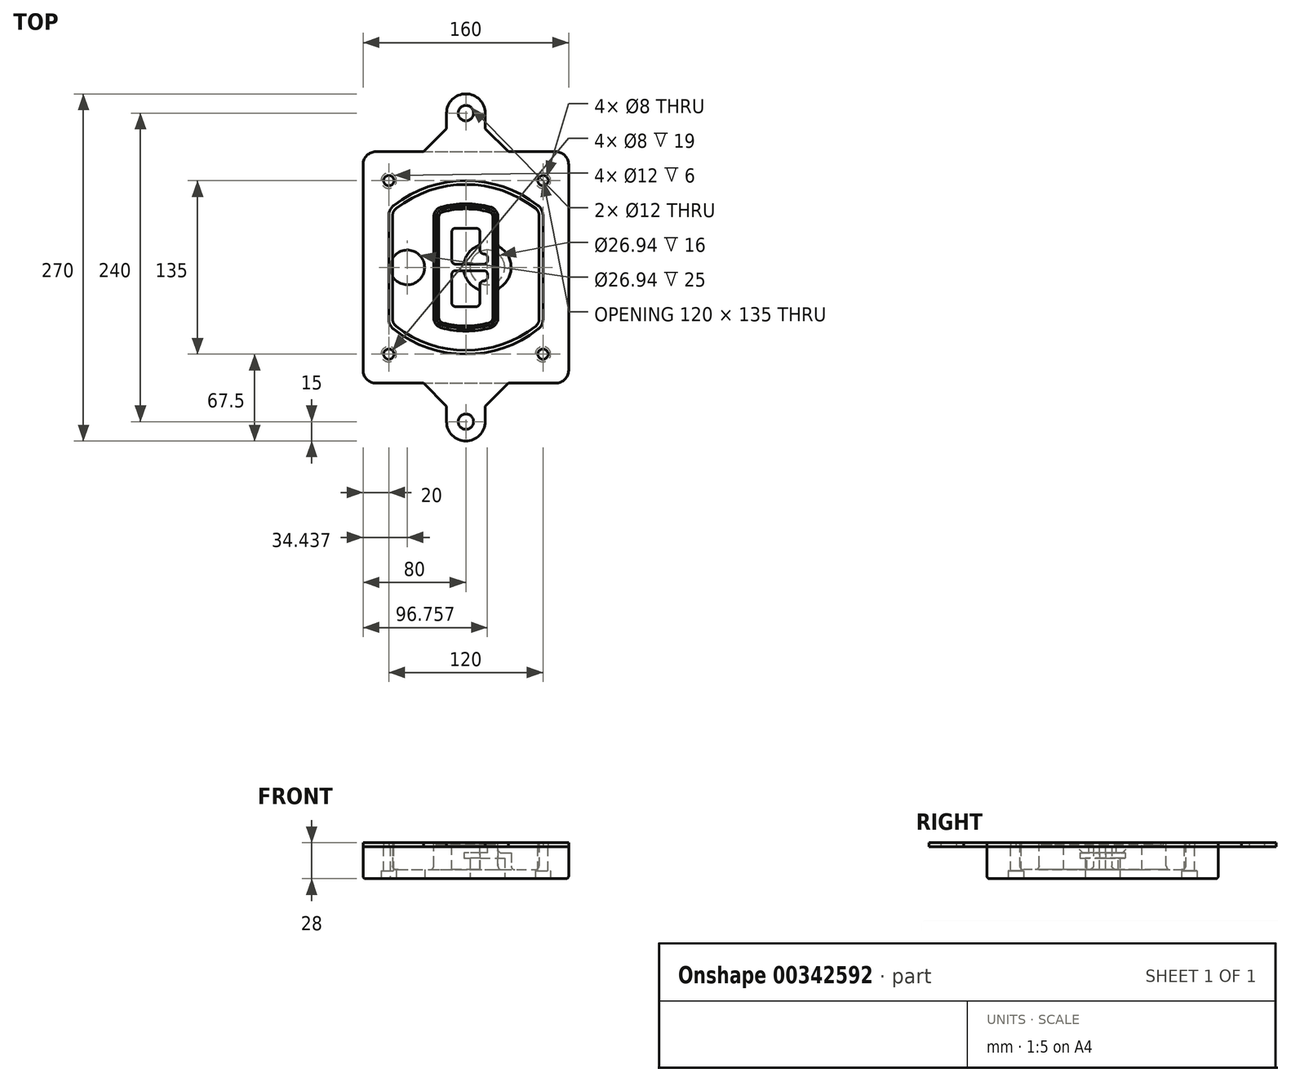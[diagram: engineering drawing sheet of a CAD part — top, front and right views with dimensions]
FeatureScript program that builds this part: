
annotation { "Feature Type Name" : "Feature", "Feature Type Description" : "" }
export const myFeature = defineFeature(function(context is Context, id is Id, definition is map)
    precondition{}
    {
        {
            var Q0;
            Q0=qCreatedBy(makeId("Top.planeOp"),FACE);
            var sketch = newSketch(context, id + "F0", { "sketchPlane" : qUnion([Q0])});
            skPoint(sketch, "E0.rect.middle", {"position": v(0, 0) * mm});
            skLineSegment(sketch, "E1.bottom", {"start": v(-70, -90) * mm, "end": v(70, -90) * mm});
            skLineSegment(sketch, "E1.top", {"start": v(-70, 90) * mm, "end": v(70, 90) * mm});
            skLineSegment(sketch, "E1.left", {"start": v(-80, -80) * mm, "end": v(-80, 80) * mm});
            skLineSegment(sketch, "E1.right", {"start": v(80, -80) * mm, "end": v(80, 80) * mm});
            skLineSegment(sketch, "E2", {"start": v(-80, 90) * mm, "end": v(80, -90) * mm, "construction": true});
            skLineSegment(sketch, "E3", {"start": v(80, 90) * mm, "end": v(-80, -90) * mm, "construction": true});
            skCircle(sketch, "E4", {"center": v(-60, 67.5) * mm, "radius": 4 * mm});
            skCircle(sketch, "E5", {"center": v(60, 67.5) * mm, "radius": 4 * mm});
            skCircle(sketch, "E6", {"center": v(60, -67.5) * mm, "radius": 4 * mm});
            skCircle(sketch, "E7", {"center": v(-60, -67.5) * mm, "radius": 4 * mm});
            skLineSegment(sketch, "E8", {"start": v(-60, 67.5) * mm, "end": v(60, 67.5) * mm, "construction": true});
            skLineSegment(sketch, "E9", {"start": v(60, 67.5) * mm, "end": v(60, -67.5) * mm, "construction": true});
            skLineSegment(sketch, "E10", {"start": v(60, -67.5) * mm, "end": v(-60, -67.5) * mm, "construction": true});
            skLineSegment(sketch, "E11", {"start": v(-60, -67.5) * mm, "end": v(-60, 67.5) * mm, "construction": true});
            skLineSegment(sketch, "E12", {"start": v(-60, 40.3) * mm, "end": v(-60, -40.3) * mm});
            skLineSegment(sketch, "E13", {"start": v(60, 40.3) * mm, "end": v(60, -40.3) * mm});
            skArc(sketch, "E14", {"start": v(56.15, 48.18) * mm, "mid": v(0, 67.5) * mm, "end": v(-56.15, 48.18) * mm});
            skArc(sketch, "E15", {"start": v(-56.15, -48.18) * mm, "mid": v(0, -67.5) * mm, "end": v(56.15, -48.18) * mm});
            skLineSegment(sketch, "E16", {"start": v(-60, 0) * mm, "end": v(60, 0) * mm, "construction": true});
            skPoint(sketch, "E17.visualSharp", {"position": v(-60, -45) * mm});
            skArc(sketch, "E17.filletArc", {"start": v(-60, -40.3) * mm, "mid": v(-58.99, -44.68) * mm, "end": v(-56.15, -48.18) * mm});
            skPoint(sketch, "E18.visualSharp", {"position": v(-60, 45) * mm});
            skArc(sketch, "E18.filletArc", {"start": v(-56.15, 48.18) * mm, "mid": v(-58.99, 44.68) * mm, "end": v(-60, 40.3) * mm});
            skPoint(sketch, "E19.visualSharp", {"position": v(60, 45) * mm});
            skArc(sketch, "E19.filletArc", {"start": v(60, 40.3) * mm, "mid": v(58.99, 44.68) * mm, "end": v(56.15, 48.18) * mm});
            skPoint(sketch, "E20.visualSharp", {"position": v(60, -45) * mm});
            skArc(sketch, "E20.filletArc", {"start": v(56.15, -48.18) * mm, "mid": v(58.99, -44.68) * mm, "end": v(60, -40.3) * mm});
            skPoint(sketch, "E21.visualSharp", {"position": v(-80, 90) * mm});
            skArc(sketch, "E21.filletArc", {"start": v(-70, 90) * mm, "mid": v(-77.07, 87.07) * mm, "end": v(-80, 80) * mm});
            skPoint(sketch, "E22.visualSharp", {"position": v(80, 90) * mm});
            skArc(sketch, "E22.filletArc", {"start": v(80, 80) * mm, "mid": v(77.07, 87.07) * mm, "end": v(70, 90) * mm});
            skPoint(sketch, "E23.visualSharp", {"position": v(80, -90) * mm});
            skArc(sketch, "E23.filletArc", {"start": v(70, -90) * mm, "mid": v(77.07, -87.07) * mm, "end": v(80, -80) * mm});
            skPoint(sketch, "E24.visualSharp", {"position": v(-80, -90) * mm});
            skArc(sketch, "E24.filletArc", {"start": v(-80, -80) * mm, "mid": v(-77.07, -87.07) * mm, "end": v(-70, -90) * mm});
            skArc(sketch, "E25.0", {"start": v(57, 40.3) * mm, "mid": v(56.3, 43.36) * mm, "end": v(54.3, 45.81) * mm});
            skLineSegment(sketch, "E25.1", {"start": v(57, 40.3) * mm, "end": v(57, -40.3) * mm});
            skArc(sketch, "E25.2", {"start": v(54.3, -45.81) * mm, "mid": v(56.3, -43.36) * mm, "end": v(57, -40.3) * mm});
            skArc(sketch, "E25.3", {"start": v(-54.3, -45.81) * mm, "mid": v(0, -64.5) * mm, "end": v(54.3, -45.81) * mm});
            skArc(sketch, "E25.4", {"start": v(-57, -40.3) * mm, "mid": v(-56.3, -43.36) * mm, "end": v(-54.3, -45.81) * mm});
            skArc(sketch, "E25.5", {"start": v(54.3, 45.81) * mm, "mid": v(0, 64.5) * mm, "end": v(-54.3, 45.81) * mm});
            skLineSegment(sketch, "E25.6", {"start": v(-57, 40.3) * mm, "end": v(-57, -40.3) * mm});
            skArc(sketch, "E25.7", {"start": v(-54.3, 45.81) * mm, "mid": v(-56.3, 43.36) * mm, "end": v(-57, 40.3) * mm});
            skArc(sketch, "E26.0", {"start": v(-58.62, 51.33) * mm, "mid": v(-62.58, 46.43) * mm, "end": v(-64, 40.3) * mm});
            skArc(sketch, "E26.1", {"start": v(58.62, 51.33) * mm, "mid": v(0, 71.5) * mm, "end": v(-58.62, 51.33) * mm});
            skArc(sketch, "E26.2", {"start": v(64, 40.3) * mm, "mid": v(62.58, 46.43) * mm, "end": v(58.62, 51.33) * mm});
            skLineSegment(sketch, "E26.3", {"start": v(64, 40.3) * mm, "end": v(64, -40.3) * mm});
            skArc(sketch, "E26.4", {"start": v(58.62, -51.33) * mm, "mid": v(62.58, -46.43) * mm, "end": v(64, -40.3) * mm});
            skLineSegment(sketch, "E26.5", {"start": v(-64, 40.3) * mm, "end": v(-64, -40.3) * mm});
            skArc(sketch, "E26.6", {"start": v(-58.62, -51.33) * mm, "mid": v(0, -71.5) * mm, "end": v(58.62, -51.33) * mm});
            skArc(sketch, "E26.7", {"start": v(-64, -40.3) * mm, "mid": v(-62.58, -46.43) * mm, "end": v(-58.62, -51.33) * mm});
            skSolve(sketch);
        }
        {
            var Q0;
            Q0=makeQuery(id+"F0.imprint","IMPRINT",FACE,{"disambiguationData":[TD([[makeQuery(id+"F0.imprint","IMPRINT",EDGE,{"derivedFrom":sQuery(id+"F0.wireOp",EDGE,"E1.bottom")}),1.0]])]});
            var Q1;
            Q1=makeQuery(id+"F0.imprint","IMPRINT",FACE,{"disambiguationData":[TD([[makeQuery(id+"F0.imprint","IMPRINT",EDGE,{"derivedFrom":sQuery(id+"F0.wireOp",EDGE,"E12")}),1.0]])]});
            var Q2;
            Q2=makeQuery(id+"F0.imprint","IMPRINT",FACE,{"disambiguationData":[TD([[makeQuery(id+"F0.imprint","IMPRINT",EDGE,{"derivedFrom":sQuery(id+"F0.wireOp",EDGE,"E25.0")}),1.0]])]});
            var Q3;
            Q3=makeQuery(id+"F0.imprint","IMPRINT",FACE,{"disambiguationData":[TD([[makeQuery(id+"F0.imprint","IMPRINT",EDGE,{"derivedFrom":sQuery(id+"F0.wireOp",EDGE,"E12")}),-1.0]])]});
            extrude(context, id + "F1", {"entities" : qUnion([Q0, Q1, Q2, Q3]), "oppositeDirection" : true, "depth" : 25 * mm});
        }
        {
            var Q0;
            Q0=makeQuery(id+"F0.imprint","IMPRINT",FACE,{"disambiguationData":[TD([[makeQuery(id+"F0.imprint","IMPRINT",EDGE,{"derivedFrom":sQuery(id+"F0.wireOp",EDGE,"E12")}),1.0]])]});
            extrude(context, id + "F2", {"entities" : qUnion([Q0]), "operationType" : NewBodyOperationType.ADD, "depth" : 3 * mm});
        }
        {
            var Q0;
            Q0=makeQuery(id+"F0.imprint","IMPRINT",FACE,{"disambiguationData":[TD([[makeQuery(id+"F0.imprint","IMPRINT",EDGE,{"derivedFrom":sQuery(id+"F0.wireOp",EDGE,"E25.0")}),1.0]])]});
            extrude(context, id + "F3", {"entities" : qUnion([Q0]), "operationType" : NewBodyOperationType.REMOVE, "oppositeDirection" : true, "depth" : 18 * mm});
        }
        {
            var Q0;
            Q0=makeQuery(id+"F2.opExtrude","CAP_FACE",FACE,{"disambiguationData":[OSD([sQuery(id+"F0.wireOp",EDGE,"E12"),sQuery(id+"F0.wireOp",EDGE,"E13"),sQuery(id+"F0.wireOp",EDGE,"E14"),sQuery(id+"F0.wireOp",EDGE,"E15"),sQuery(id+"F0.wireOp",EDGE,"E17.filletArc"),sQuery(id+"F0.wireOp",EDGE,"E18.filletArc"),sQuery(id+"F0.wireOp",EDGE,"E19.filletArc"),sQuery(id+"F0.wireOp",EDGE,"E20.filletArc"),sQuery(id+"F0.wireOp",EDGE,"E25.0"),sQuery(id+"F0.wireOp",EDGE,"E25.1"),sQuery(id+"F0.wireOp",EDGE,"E25.2"),sQuery(id+"F0.wireOp",EDGE,"E25.3"),sQuery(id+"F0.wireOp",EDGE,"E25.4"),sQuery(id+"F0.wireOp",EDGE,"E25.5"),sQuery(id+"F0.wireOp",EDGE,"E25.6"),sQuery(id+"F0.wireOp",EDGE,"E25.7")])],"isStart":false});
            var sketch = newSketch(context, id + "F4", { "sketchPlane" : qUnion([Q0])});
            skArc(sketch, "E27.0", {"start": v(-19.08, -46.97) * mm, "mid": v(0, -49.5) * mm, "end": v(19.08, -46.97) * mm});
            skArc(sketch, "E28.0", {"start": v(19.08, 46.97) * mm, "mid": v(0, 49.5) * mm, "end": v(-19.08, 46.97) * mm});
            skLineSegment(sketch, "E29", {"start": v(-25, 39.25) * mm, "end": v(-25, -39.25) * mm});
            skLineSegment(sketch, "E30", {"start": v(25, 39.25) * mm, "end": v(25, -39.25) * mm});
            skLineSegment(sketch, "E31", {"start": v(-25, 45.1) * mm, "end": v(25, 45.1) * mm, "construction": true});
            skLineSegment(sketch, "E32", {"start": v(-25, -45.1) * mm, "end": v(25, -45.1) * mm, "construction": true});
            skPoint(sketch, "E33.visualSharp", {"position": v(-25, 45.1) * mm});
            skArc(sketch, "E33.filletArc", {"start": v(-19.08, 46.97) * mm, "mid": v(-23.35, 44.11) * mm, "end": v(-25, 39.25) * mm});
            skPoint(sketch, "E34.visualSharp", {"position": v(25, 45.1) * mm});
            skArc(sketch, "E34.filletArc", {"start": v(25, 39.25) * mm, "mid": v(23.35, 44.11) * mm, "end": v(19.08, 46.97) * mm});
            skPoint(sketch, "E35.visualSharp", {"position": v(25, -45.1) * mm});
            skArc(sketch, "E35.filletArc", {"start": v(19.08, -46.97) * mm, "mid": v(23.35, -44.11) * mm, "end": v(25, -39.25) * mm});
            skPoint(sketch, "E36.visualSharp", {"position": v(-25, -45.1) * mm});
            skArc(sketch, "E36.filletArc", {"start": v(-25, -39.25) * mm, "mid": v(-23.35, -44.11) * mm, "end": v(-19.08, -46.97) * mm});
            skArc(sketch, "E37.0", {"start": v(54.3, 45.81) * mm, "mid": v(0, 64.5) * mm, "end": v(-54.3, 45.81) * mm});
            skArc(sketch, "E37.1", {"start": v(-54.3, 45.81) * mm, "mid": v(-56.3, 43.36) * mm, "end": v(-57, 40.3) * mm});
            skLineSegment(sketch, "E37.2", {"start": v(-57, 40.3) * mm, "end": v(-57, -40.3) * mm});
            skArc(sketch, "E37.3", {"start": v(-57, -40.3) * mm, "mid": v(-56.3, -43.36) * mm, "end": v(-54.3, -45.81) * mm});
            skArc(sketch, "E37.4", {"start": v(-54.3, -45.81) * mm, "mid": v(0, -64.5) * mm, "end": v(54.3, -45.81) * mm});
            skArc(sketch, "E37.5", {"start": v(54.3, -45.81) * mm, "mid": v(56.3, -43.36) * mm, "end": v(57, -40.3) * mm});
            skLineSegment(sketch, "E37.6", {"start": v(57, 40.3) * mm, "end": v(57, -40.3) * mm});
            skArc(sketch, "E37.7", {"start": v(57, 40.3) * mm, "mid": v(56.3, 43.36) * mm, "end": v(54.3, 45.81) * mm});
            skLineSegment(sketch, "E38.0", {"start": v(23, 39.25) * mm, "end": v(23, -39.25) * mm});
            skArc(sketch, "E38.1", {"start": v(18.56, -45.04) * mm, "mid": v(21.76, -42.9) * mm, "end": v(23, -39.25) * mm});
            skArc(sketch, "E38.2", {"start": v(-18.56, -45.04) * mm, "mid": v(0, -47.5) * mm, "end": v(18.56, -45.04) * mm});
            skArc(sketch, "E38.3", {"start": v(-23, -39.25) * mm, "mid": v(-21.76, -42.9) * mm, "end": v(-18.56, -45.04) * mm});
            skLineSegment(sketch, "E38.4", {"start": v(-23, 39.25) * mm, "end": v(-23, -39.25) * mm});
            skArc(sketch, "E38.5", {"start": v(23, 39.25) * mm, "mid": v(21.76, 42.9) * mm, "end": v(18.56, 45.04) * mm});
            skArc(sketch, "E38.6", {"start": v(-18.56, 45.04) * mm, "mid": v(-21.76, 42.9) * mm, "end": v(-23, 39.25) * mm});
            skArc(sketch, "E38.7", {"start": v(18.56, 45.04) * mm, "mid": v(0, 47.5) * mm, "end": v(-18.56, 45.04) * mm});
            skArc(sketch, "E39.0", {"start": v(21, 39.25) * mm, "mid": v(20.18, 41.68) * mm, "end": v(18.04, 43.1) * mm});
            skLineSegment(sketch, "E39.1", {"start": v(21, 39.25) * mm, "end": v(21, -39.25) * mm});
            skArc(sketch, "E39.2", {"start": v(18.04, -43.1) * mm, "mid": v(20.18, -41.68) * mm, "end": v(21, -39.25) * mm});
            skArc(sketch, "E39.3", {"start": v(-18.04, -43.1) * mm, "mid": v(0, -45.5) * mm, "end": v(18.04, -43.1) * mm});
            skArc(sketch, "E39.4", {"start": v(-21, -39.25) * mm, "mid": v(-20.18, -41.68) * mm, "end": v(-18.04, -43.1) * mm});
            skArc(sketch, "E39.5", {"start": v(18.04, 43.1) * mm, "mid": v(0, 45.5) * mm, "end": v(-18.04, 43.1) * mm});
            skLineSegment(sketch, "E39.6", {"start": v(-21, 39.25) * mm, "end": v(-21, -39.25) * mm});
            skArc(sketch, "E39.7", {"start": v(-18.04, 43.1) * mm, "mid": v(-20.18, 41.68) * mm, "end": v(-21, 39.25) * mm});
            skLineSegment(sketch, "E40", {"start": v(-25, 0) * mm, "end": v(25, 0) * mm, "construction": true});
            skLineSegment(sketch, "E41", {"start": v(-11, 5.5) * mm, "end": v(-11, 27.5) * mm});
            skLineSegment(sketch, "E42", {"start": v(-8, 30.5) * mm, "end": v(8, 30.5) * mm});
            skLineSegment(sketch, "E43", {"start": v(11, 27.5) * mm, "end": v(11, 13.5) * mm});
            skLineSegment(sketch, "E44", {"start": v(14, 10.5) * mm, "end": v(14, 10.5) * mm});
            skLineSegment(sketch, "E45", {"start": v(17, 7.5) * mm, "end": v(17, 5.5) * mm});
            skLineSegment(sketch, "E46", {"start": v(14, 2.5) * mm, "end": v(-8, 2.5) * mm});
            skPoint(sketch, "E47.visualSharp", {"position": v(-11, 30.5) * mm});
            skArc(sketch, "E47.filletArc", {"start": v(-8, 30.5) * mm, "mid": v(-10.12, 29.62) * mm, "end": v(-11, 27.5) * mm});
            skPoint(sketch, "E48.visualSharp", {"position": v(11, 30.5) * mm});
            skArc(sketch, "E48.filletArc", {"start": v(11, 27.5) * mm, "mid": v(10.12, 29.62) * mm, "end": v(8, 30.5) * mm});
            skPoint(sketch, "E49.visualSharp", {"position": v(11, 10.5) * mm});
            skArc(sketch, "E49.filletArc", {"start": v(11, 13.5) * mm, "mid": v(11.88, 11.38) * mm, "end": v(14, 10.5) * mm});
            skPoint(sketch, "E50.visualSharp", {"position": v(17, 10.5) * mm});
            skArc(sketch, "E50.filletArc", {"start": v(17, 7.5) * mm, "mid": v(16.12, 9.62) * mm, "end": v(14, 10.5) * mm});
            skPoint(sketch, "E51.visualSharp", {"position": v(17, 2.5) * mm});
            skArc(sketch, "E51.filletArc", {"start": v(14, 2.5) * mm, "mid": v(16.12, 3.38) * mm, "end": v(17, 5.5) * mm});
            skPoint(sketch, "E52.visualSharp", {"position": v(-11, 2.5) * mm});
            skArc(sketch, "E52.filletArc", {"start": v(-11, 5.5) * mm, "mid": v(-10.12, 3.38) * mm, "end": v(-8, 2.5) * mm});
            skLineSegment(sketch, "E53.0.MirrorCS", {"start": v(14, -2.5) * mm, "end": v(-8, -2.5) * mm});
            skArc(sketch, "E54.0.MirrorCS", {"start": v(-11, -5.5) * mm, "mid": v(-10.12, -3.38) * mm, "end": v(-8, -2.5) * mm});
            skLineSegment(sketch, "E55.0.MirrorCS", {"start": v(-11, -5.5) * mm, "end": v(-11, -27.5) * mm});
            skArc(sketch, "E56.0.MirrorCS", {"start": v(-8, -30.5) * mm, "mid": v(-10.12, -29.62) * mm, "end": v(-11, -27.5) * mm});
            skLineSegment(sketch, "E57.0.MirrorCS", {"start": v(-8, -30.5) * mm, "end": v(8, -30.5) * mm});
            skArc(sketch, "E58.0.MirrorCS", {"start": v(11, -27.5) * mm, "mid": v(10.12, -29.62) * mm, "end": v(8, -30.5) * mm});
            skLineSegment(sketch, "E59.0.MirrorCS", {"start": v(11, -27.5) * mm, "end": v(11, -13.5) * mm});
            skArc(sketch, "E60.0.MirrorCS", {"start": v(11, -13.5) * mm, "mid": v(11.88, -11.38) * mm, "end": v(14, -10.5) * mm});
            skArc(sketch, "E61.0.MirrorCS", {"start": v(17, -7.5) * mm, "mid": v(16.12, -9.62) * mm, "end": v(14, -10.5) * mm});
            skLineSegment(sketch, "E62.0.MirrorCS", {"start": v(17, -7.5) * mm, "end": v(17, -5.5) * mm});
            skArc(sketch, "E63.0.MirrorCS", {"start": v(14, -2.5) * mm, "mid": v(16.12, -3.38) * mm, "end": v(17, -5.5) * mm});
            skSolve(sketch);
        }
        {
            var Q0;
            Q0=makeQuery(id+"F4.imprint","IMPRINT",FACE,{"disambiguationData":[TD([[makeQuery(id+"F4.imprint","IMPRINT",EDGE,{"derivedFrom":sQuery(id+"F4.wireOp",EDGE,"E27.0")}),1.0]])]});
            var Q1;
            Q1=makeQuery(id+"F4.imprint","IMPRINT",FACE,{"disambiguationData":[TD([[makeQuery(id+"F4.imprint","IMPRINT",EDGE,{"derivedFrom":sQuery(id+"F4.wireOp",EDGE,"E38.0")}),-1.0]])]});
            var Q2;
            Q2=makeQuery(id+"F4.imprint","IMPRINT",FACE,{"disambiguationData":[TD([[makeQuery(id+"F4.imprint","IMPRINT",EDGE,{"derivedFrom":sQuery(id+"F4.wireOp",EDGE,"E39.0")}),1.0]])]});
            extrude(context, id + "F5", {"entities" : qUnion([Q0, Q1, Q2]), "operationType" : NewBodyOperationType.ADD, "endBound" : BoundingType.UP_TO_NEXT, "oppositeDirection" : true, "depth" : 25 * mm});
        }
        {
            var Q0;
            Q0=makeQuery(id+"F4.imprint","IMPRINT",FACE,{"disambiguationData":[TD([[makeQuery(id+"F4.imprint","IMPRINT",EDGE,{"derivedFrom":sQuery(id+"F4.wireOp",EDGE,"E38.0")}),-1.0]])]});
            extrude(context, id + "F6", {"entities" : qUnion([Q0]), "operationType" : NewBodyOperationType.REMOVE, "oppositeDirection" : true, "depth" : 2 * mm});
        }
        {
            var Q0;
            Q0=makeQuery(id+"F1.opExtrude","CAP_FACE",FACE,{"disambiguationData":[OSD([sQuery(id+"F0.wireOp",EDGE,"E1.bottom"),sQuery(id+"F0.wireOp",EDGE,"E1.top"),sQuery(id+"F0.wireOp",EDGE,"E1.left"),sQuery(id+"F0.wireOp",EDGE,"E1.right"),sQuery(id+"F0.wireOp",EDGE,"E4"),sQuery(id+"F0.wireOp",EDGE,"E5"),sQuery(id+"F0.wireOp",EDGE,"E6"),sQuery(id+"F0.wireOp",EDGE,"E7"),sQuery(id+"F0.wireOp",EDGE,"E21.filletArc"),sQuery(id+"F0.wireOp",EDGE,"E22.filletArc"),sQuery(id+"F0.wireOp",EDGE,"E23.filletArc"),sQuery(id+"F0.wireOp",EDGE,"E24.filletArc")])],"isStart":false});
            var sketch = newSketch(context, id + "F7", { "sketchPlane" : qUnion([Q0])});
            skCircle(sketch, "E64", {"center": v(16.76, 0) * mm, "radius": 13.47 * mm});
            skCircle(sketch, "E65", {"center": v(-45.56, 0) * mm, "radius": 13.47 * mm});
            skLineSegment(sketch, "E66", {"start": v(80, 0) * mm, "end": v(-80, 0) * mm});
            skCircle(sketch, "E67", {"center": v(16.76, 0) * mm, "radius": 18.47 * mm});
            skCircle(sketch, "E68", {"center": v(60, -67.5) * mm, "radius": 6 * mm});
            skCircle(sketch, "E69", {"center": v(-60, -67.5) * mm, "radius": 6 * mm});
            skCircle(sketch, "E70", {"center": v(-60, 67.5) * mm, "radius": 6 * mm});
            skCircle(sketch, "E71", {"center": v(60, 67.5) * mm, "radius": 6 * mm});
            skSolve(sketch);
        }
        {
            var Q0;
            {var subQ1=sQuery(id+"F7.wireOp",EDGE,"E66");var subQ4=sQuery(id+"F7.wireOp",EDGE,"E64");var subQ6=makeQuery(id+"F7.imprint","INTERSECT",VERTEX,{"disambiguationData":[OD(0.0)],"derivedFrom":[subQ4,subQ1]});Q0=makeQuery(id+"F7.imprint","IMPRINT",FACE,{"disambiguationData":[TD([[makeQuery(id+"F7.imprint","IMPRINT",EDGE,{"disambiguationData":[TD([[subQ6,-1.0]])],"derivedFrom":subQ4}),-1.0]])]});}
            var Q1;
            {var subQ0=sQuery(id+"F7.wireOp",EDGE,"E66");var subQ1=sQuery(id+"F7.wireOp",EDGE,"E64");var subQ3=makeQuery(id+"F7.imprint","INTERSECT",VERTEX,{"disambiguationData":[OD(0.0)],"derivedFrom":[subQ1,subQ0]});Q1=makeQuery(id+"F7.imprint","IMPRINT",FACE,{"disambiguationData":[TD([[makeQuery(id+"F7.imprint","IMPRINT",EDGE,{"disambiguationData":[TD([[subQ3,-1.0]])],"derivedFrom":subQ1}),1.0]])]});}
            var Q2;
            {var subQ0=sQuery(id+"F7.wireOp",EDGE,"E66");var subQ1=sQuery(id+"F7.wireOp",EDGE,"E64");var subQ3=makeQuery(id+"F7.imprint","INTERSECT",VERTEX,{"disambiguationData":[OD(0.0)],"derivedFrom":[subQ1,subQ0]});Q2=makeQuery(id+"F7.imprint","IMPRINT",FACE,{"disambiguationData":[TD([[makeQuery(id+"F7.imprint","IMPRINT",EDGE,{"disambiguationData":[TD([[subQ3,1.0]])],"derivedFrom":subQ1}),1.0]])]});}
            var Q3;
            {var subQ1=sQuery(id+"F7.wireOp",EDGE,"E66");var subQ4=sQuery(id+"F7.wireOp",EDGE,"E64");var subQ6=makeQuery(id+"F7.imprint","INTERSECT",VERTEX,{"disambiguationData":[OD(0.0)],"derivedFrom":[subQ4,subQ1]});Q3=makeQuery(id+"F7.imprint","IMPRINT",FACE,{"disambiguationData":[TD([[makeQuery(id+"F7.imprint","IMPRINT",EDGE,{"disambiguationData":[TD([[subQ6,1.0]])],"derivedFrom":subQ4}),-1.0]])]});}
            extrude(context, id + "F8", {"entities" : qUnion([Q0, Q1, Q2, Q3]), "operationType" : NewBodyOperationType.ADD, "oppositeDirection" : true, "depth" : 20 * mm});
        }
        {
            var Q0;
            {var subQ0=sQuery(id+"F7.wireOp",EDGE,"E66");var subQ1=sQuery(id+"F7.wireOp",EDGE,"E64");var subQ3=makeQuery(id+"F7.imprint","INTERSECT",VERTEX,{"disambiguationData":[OD(0.0)],"derivedFrom":[subQ1,subQ0]});Q0=makeQuery(id+"F7.imprint","IMPRINT",FACE,{"disambiguationData":[TD([[makeQuery(id+"F7.imprint","IMPRINT",EDGE,{"disambiguationData":[TD([[subQ3,-1.0]])],"derivedFrom":subQ1}),1.0]])]});}
            var Q1;
            {var subQ0=sQuery(id+"F7.wireOp",EDGE,"E66");var subQ1=sQuery(id+"F7.wireOp",EDGE,"E64");var subQ3=makeQuery(id+"F7.imprint","INTERSECT",VERTEX,{"disambiguationData":[OD(0.0)],"derivedFrom":[subQ1,subQ0]});Q1=makeQuery(id+"F7.imprint","IMPRINT",FACE,{"disambiguationData":[TD([[makeQuery(id+"F7.imprint","IMPRINT",EDGE,{"disambiguationData":[TD([[subQ3,1.0]])],"derivedFrom":subQ1}),1.0]])]});}
            extrude(context, id + "F9", {"entities" : qUnion([Q0, Q1]), "operationType" : NewBodyOperationType.REMOVE, "oppositeDirection" : true, "depth" : 16 * mm});
        }
        {
            var Q0;
            {var subQ0=sQuery(id+"F7.wireOp",EDGE,"E66");var subQ1=sQuery(id+"F7.wireOp",EDGE,"E65");var subQ3=makeQuery(id+"F7.imprint","INTERSECT",VERTEX,{"disambiguationData":[OD(0.0)],"derivedFrom":[subQ1,subQ0]});Q0=makeQuery(id+"F7.imprint","IMPRINT",FACE,{"disambiguationData":[TD([[makeQuery(id+"F7.imprint","IMPRINT",EDGE,{"disambiguationData":[TD([[subQ3,-1.0]])],"derivedFrom":subQ1}),1.0]])]});}
            var Q1;
            {var subQ0=sQuery(id+"F7.wireOp",EDGE,"E66");var subQ1=sQuery(id+"F7.wireOp",EDGE,"E65");var subQ3=makeQuery(id+"F7.imprint","INTERSECT",VERTEX,{"disambiguationData":[OD(0.0)],"derivedFrom":[subQ1,subQ0]});Q1=makeQuery(id+"F7.imprint","IMPRINT",FACE,{"disambiguationData":[TD([[makeQuery(id+"F7.imprint","IMPRINT",EDGE,{"disambiguationData":[TD([[subQ3,1.0]])],"derivedFrom":subQ1}),1.0]])]});}
            extrude(context, id + "F10", {"entities" : qUnion([Q0, Q1]), "operationType" : NewBodyOperationType.REMOVE, "oppositeDirection" : true, "depth" : 25 * mm});
        }
        {
            var Q0;
            Q0=makeQuery(id+"F7.imprint","IMPRINT",FACE,{"disambiguationData":[TD([[makeQuery(id+"F7.imprint","IMPRINT",EDGE,{"derivedFrom":sQuery(id+"F7.wireOp",EDGE,"E68")}),1.0]])]});
            var Q1;
            Q1=makeQuery(id+"F7.imprint","IMPRINT",FACE,{"disambiguationData":[TD([[makeQuery(id+"F7.imprint","IMPRINT",EDGE,{"derivedFrom":makeQuery(id+"F1.opExtrude","CAP_EDGE",EDGE,{"disambiguationData":[OSD([sQuery(id+"F0.wireOp",EDGE,"E5")])],"isStart":false})}),-1.0]])]});
            var Q2;
            Q2=makeQuery(id+"F7.imprint","IMPRINT",FACE,{"disambiguationData":[TD([[makeQuery(id+"F7.imprint","IMPRINT",EDGE,{"derivedFrom":sQuery(id+"F7.wireOp",EDGE,"E69")}),1.0]])]});
            var Q3;
            Q3=makeQuery(id+"F7.imprint","IMPRINT",FACE,{"disambiguationData":[TD([[makeQuery(id+"F7.imprint","IMPRINT",EDGE,{"derivedFrom":makeQuery(id+"F1.opExtrude","CAP_EDGE",EDGE,{"disambiguationData":[OSD([sQuery(id+"F0.wireOp",EDGE,"E4")])],"isStart":false})}),-1.0]])]});
            var Q4;
            Q4=makeQuery(id+"F7.imprint","IMPRINT",FACE,{"disambiguationData":[TD([[makeQuery(id+"F7.imprint","IMPRINT",EDGE,{"derivedFrom":sQuery(id+"F7.wireOp",EDGE,"E70")}),1.0]])]});
            var Q5;
            Q5=makeQuery(id+"F7.imprint","IMPRINT",FACE,{"disambiguationData":[TD([[makeQuery(id+"F7.imprint","IMPRINT",EDGE,{"derivedFrom":makeQuery(id+"F1.opExtrude","CAP_EDGE",EDGE,{"disambiguationData":[OSD([sQuery(id+"F0.wireOp",EDGE,"E7")])],"isStart":false})}),-1.0]])]});
            var Q6;
            Q6=makeQuery(id+"F7.imprint","IMPRINT",FACE,{"disambiguationData":[TD([[makeQuery(id+"F7.imprint","IMPRINT",EDGE,{"derivedFrom":sQuery(id+"F7.wireOp",EDGE,"E71")}),1.0]])]});
            var Q7;
            Q7=makeQuery(id+"F7.imprint","IMPRINT",FACE,{"disambiguationData":[TD([[makeQuery(id+"F7.imprint","IMPRINT",EDGE,{"derivedFrom":makeQuery(id+"F1.opExtrude","CAP_EDGE",EDGE,{"disambiguationData":[OSD([sQuery(id+"F0.wireOp",EDGE,"E6")])],"isStart":false})}),-1.0]])]});
            extrude(context, id + "F11", {"entities" : qUnion([Q0, Q1, Q2, Q3, Q4, Q5, Q6, Q7]), "operationType" : NewBodyOperationType.REMOVE, "oppositeDirection" : true, "depth" : 6 * mm});
        }
        {
            var Q0;
            Q0=makeQuery(id+"F9.boolean.opBoolean","COPY",FACE,{"derivedFrom":makeQuery(id+"F9.opExtrude","CAP_FACE",FACE,{"disambiguationData":[OSD([sQuery(id+"F7.wireOp",EDGE,"E64")])],"isStart":false})});
            var sketch = newSketch(context, id + "F12", { "sketchPlane" : qUnion([Q0])});
            skArc(sketch, "E72.0", {"start": v(11, 17.55) * mm, "mid": v(2.57, 11.82) * mm, "end": v(-1.54, 2.5) * mm});
            skArc(sketch, "E72.1", {"start": v(-1.54, -2.5) * mm, "mid": v(2.57, -11.82) * mm, "end": v(11, -17.55) * mm});
            skLineSegment(sketch, "E73", {"start": v(-1.54, -2.5) * mm, "end": v(14, -2.5) * mm});
            skLineSegment(sketch, "E74.0", {"start": v(14, 2.5) * mm, "end": v(-1.54, 2.5) * mm});
            skArc(sketch, "E74.1", {"start": v(14, 2.5) * mm, "mid": v(16.12, 3.38) * mm, "end": v(17, 5.5) * mm});
            skLineSegment(sketch, "E74.2", {"start": v(17, 7.5) * mm, "end": v(17, 5.5) * mm});
            skArc(sketch, "E74.3", {"start": v(17, 7.5) * mm, "mid": v(16.12, 9.62) * mm, "end": v(14, 10.5) * mm});
            skArc(sketch, "E74.4", {"start": v(11, 13.5) * mm, "mid": v(11.88, 11.38) * mm, "end": v(14, 10.5) * mm});
            skLineSegment(sketch, "E74.5", {"start": v(11, 17.55) * mm, "end": v(11, 13.5) * mm});
            skLineSegment(sketch, "E74.7", {"start": v(14, -2.5) * mm, "end": v(-1.54, -2.5) * mm});
            skArc(sketch, "E74.8", {"start": v(14, -2.5) * mm, "mid": v(16.12, -3.38) * mm, "end": v(17, -5.5) * mm});
            skLineSegment(sketch, "E74.9", {"start": v(17, -7.5) * mm, "end": v(17, -5.5) * mm});
            skArc(sketch, "E74.10", {"start": v(17, -7.5) * mm, "mid": v(16.12, -9.62) * mm, "end": v(14, -10.5) * mm});
            skArc(sketch, "E74.11", {"start": v(11, -13.5) * mm, "mid": v(11.88, -11.38) * mm, "end": v(14, -10.5) * mm});
            skLineSegment(sketch, "E74.12", {"start": v(11, -17.55) * mm, "end": v(11, -13.5) * mm});
            skPoint(sketch, "E75.orphan", {"position": v(11, -27.5) * mm});
            skPoint(sketch, "E76.orphan", {"position": v(-8, -2.5) * mm});
            skPoint(sketch, "E77.orphan", {"position": v(-8, 2.5) * mm});
            skPoint(sketch, "E78.orphan", {"position": v(11, 27.5) * mm});
            skSolve(sketch);
        }
        {
            var Q0;
            {var subQ7=sQuery(id+"F12.wireOp",EDGE,"E72.0");var subQ14=sQuery(id+"F12.wireOp",EDGE,"E72.1");var subQ16=sQuery(id+"F12.wireOp",EDGE,"E74.1");var subQ18=sQuery(id+"F12.wireOp",EDGE,"E74.8");Q0=qUnion([makeQuery(id+"F12.imprint","IMPRINT",FACE,{"disambiguationData":[TD([[makeQuery(id+"F12.imprint","IMPRINT",EDGE,{"derivedFrom":subQ7}),1.0]])]}),makeQuery(id+"F12.imprint","IMPRINT",FACE,{"disambiguationData":[TD([[makeQuery(id+"F12.imprint","IMPRINT",EDGE,{"derivedFrom":subQ14}),1.0]])]}),makeQuery(id+"F12.imprint","IMPRINT",FACE,{"disambiguationData":[TD([[makeQuery(id+"F12.imprint","IMPRINT",EDGE,{"derivedFrom":subQ16}),1.0]])]}),makeQuery(id+"F12.imprint","IMPRINT",FACE,{"disambiguationData":[TD([[makeQuery(id+"F12.imprint","IMPRINT",EDGE,{"derivedFrom":subQ18}),-1.0]])]})]);}
            var Q1;
            Q1=makeQuery(id+"F5.boolean.opBoolean","SPLIT",FACE,{"disambiguationData":[TD([makeQuery(id+"F5.opExtrude","SWEPT_FACE",FACE,{"disambiguationData":[OSD([sQuery(id+"F4.wireOp",EDGE,"E41")])]})])],"derivedFrom":makeQuery(id+"F3.boolean.opBoolean","COPY",FACE,{"derivedFrom":makeQuery(id+"F3.opExtrude","CAP_FACE",FACE,{"disambiguationData":[OSD([sQuery(id+"F0.wireOp",EDGE,"E25.0"),sQuery(id+"F0.wireOp",EDGE,"E25.1"),sQuery(id+"F0.wireOp",EDGE,"E25.2"),sQuery(id+"F0.wireOp",EDGE,"E25.3"),sQuery(id+"F0.wireOp",EDGE,"E25.4"),sQuery(id+"F0.wireOp",EDGE,"E25.5"),sQuery(id+"F0.wireOp",EDGE,"E25.6"),sQuery(id+"F0.wireOp",EDGE,"E25.7")])],"isStart":false})})});
            extrude(context, id + "F13", {"entities" : qUnion([Q0]), "operationType" : NewBodyOperationType.REMOVE, "endBound" : BoundingType.UP_TO_SURFACE, "endBoundEntityFace" : qUnion([Q1]), "depth" : 25 * mm});
        }
        {
            var Q0;
            Q0=makeQuery(id+"F3.boolean.opBoolean","COPY",EDGE,{"derivedFrom":makeQuery(id+"F3.opExtrude","CAP_EDGE",EDGE,{"disambiguationData":[OSD([sQuery(id+"F0.wireOp",EDGE,"E25.6")])],"isStart":false})});
            var Q1;
            Q1=makeQuery(id+"F8.boolean.opBoolean","INTERSECT",EDGE,{"derivedFrom":[makeQuery(id+"F5.opExtrude","SWEPT_FACE",FACE,{"disambiguationData":[OSD([sQuery(id+"F4.wireOp",EDGE,"E30")])]}),makeQuery(id+"F8.opExtrude","CAP_FACE",FACE,{"disambiguationData":[OSD([sQuery(id+"F7.wireOp",EDGE,"E67")])],"isStart":false})]});
            var Q2;
            Q2=makeQuery(id+"F8.boolean.opBoolean","INTERSECT",EDGE,{"disambiguationData":[OD(1.0)],"derivedFrom":[makeQuery(id+"F5.opExtrude","SWEPT_FACE",FACE,{"disambiguationData":[OSD([sQuery(id+"F4.wireOp",EDGE,"E30")])]}),makeQuery(id+"F8.opExtrude","SWEPT_FACE",FACE,{"disambiguationData":[OSD([sQuery(id+"F7.wireOp",EDGE,"E67")])]})]});
            var Q3;
            {var subQ0=sQuery(id+"F4.wireOp",EDGE,"E30");Q3=makeQuery(id+"F8.boolean.opBoolean","SPLIT",EDGE,{"disambiguationData":[TD([makeQuery(id+"F5.opExtrude","SWEPT_FACE",FACE,{"disambiguationData":[OSD([sQuery(id+"F4.wireOp",EDGE,"E35.filletArc")])]})])],"derivedFrom":makeQuery(id+"F5.opExtrude","CAP_EDGE",EDGE,{"disambiguationData":[OSD([subQ0])],"isStart":false})});}
            var Q4;
            {var subQ0=sQuery(id+"F0.wireOp",EDGE,"E25.7");var subQ1=sQuery(id+"F0.wireOp",EDGE,"E25.1");var subQ2=sQuery(id+"F0.wireOp",EDGE,"E25.6");var subQ3=sQuery(id+"F0.wireOp",EDGE,"E25.5");var subQ4=sQuery(id+"F0.wireOp",EDGE,"E25.4");var subQ5=sQuery(id+"F0.wireOp",EDGE,"E25.0");var subQ6=sQuery(id+"F0.wireOp",EDGE,"E25.2");var subQ7=sQuery(id+"F0.wireOp",EDGE,"E25.3");Q4=makeQuery(id+"F8.boolean.opBoolean","INTERSECT",EDGE,{"derivedFrom":[makeQuery(id+"F5.boolean.opBoolean","SPLIT",FACE,{"disambiguationData":[TD([makeQuery(id+"F2.opExtrude","SWEPT_FACE",FACE,{"disambiguationData":[OSD([subQ5])]})])],"derivedFrom":makeQuery(id+"F3.boolean.opBoolean","COPY",FACE,{"derivedFrom":makeQuery(id+"F3.opExtrude","CAP_FACE",FACE,{"disambiguationData":[OSD([subQ5,subQ1,subQ6,subQ7,subQ4,subQ3,subQ2,subQ0])],"isStart":false})})}),makeQuery(id+"F8.opExtrude","SWEPT_FACE",FACE,{"disambiguationData":[OSD([sQuery(id+"F7.wireOp",EDGE,"E67")])]})]});}
            var Q5;
            Q5=makeQuery(id+"F8.boolean.opBoolean","INTERSECT",EDGE,{"disambiguationData":[OD(0.0)],"derivedFrom":[makeQuery(id+"F5.opExtrude","SWEPT_FACE",FACE,{"disambiguationData":[OSD([sQuery(id+"F4.wireOp",EDGE,"E30")])]}),makeQuery(id+"F8.opExtrude","SWEPT_FACE",FACE,{"disambiguationData":[OSD([sQuery(id+"F7.wireOp",EDGE,"E67")])]})]});
            fillet(context, id + "F14", {"entities" : qUnion([Q0, Q1, Q2, Q3, Q4, Q5]), "radius" : 3 * mm, "tangentPropagation" : true, "allowEdgeOverflow" : false});
        }
        {
            var Q0;
            Q0=makeQuery(id+"F1.opExtrude","CAP_EDGE",EDGE,{"disambiguationData":[OSD([sQuery(id+"F0.wireOp",EDGE,"E1.bottom")])],"isStart":false});
            fillet(context, id + "F15", {"entities" : qUnion([Q0]), "radius" : 2 * mm, "tangentPropagation" : true, "allowEdgeOverflow" : false});
        }
        {
            var Q0;
            {var subQ0=sQuery(id+"F0.wireOp",EDGE,"E21.filletArc");var subQ1=sQuery(id+"F0.wireOp",EDGE,"E7");var subQ2=sQuery(id+"F0.wireOp",EDGE,"E6");var subQ3=sQuery(id+"F0.wireOp",EDGE,"E5");var subQ4=sQuery(id+"F0.wireOp",EDGE,"E4");var subQ5=sQuery(id+"F0.wireOp",EDGE,"E22.filletArc");var subQ6=sQuery(id+"F0.wireOp",EDGE,"E1.bottom");var subQ7=sQuery(id+"F0.wireOp",EDGE,"E1.right");var subQ8=sQuery(id+"F0.wireOp",EDGE,"E1.top");var subQ9=sQuery(id+"F0.wireOp",EDGE,"E1.left");var subQ10=sQuery(id+"F0.wireOp",EDGE,"E23.filletArc");var subQ11=sQuery(id+"F0.wireOp",EDGE,"E24.filletArc");Q0=makeQuery(id+"F2.boolean.opBoolean","SPLIT",FACE,{"disambiguationData":[TD([makeQuery(id+"F1.opExtrude","SWEPT_FACE",FACE,{"disambiguationData":[OSD([subQ6])]})])],"derivedFrom":makeQuery(id+"F1.opExtrude","CAP_FACE",FACE,{"disambiguationData":[OSD([subQ6,subQ8,subQ9,subQ7,subQ4,subQ3,subQ2,subQ1,subQ0,subQ5,subQ10,subQ11])],"isStart":true})});}
            var sketch = newSketch(context, id + "F16", { "sketchPlane" : qUnion([Q0])});
            skLineSegment(sketch, "E79.0", {"start": v(-70, 90) * mm, "end": v(70, 90) * mm});
            skArc(sketch, "E79.1", {"start": v(-70, 90) * mm, "mid": v(-77.07, 87.07) * mm, "end": v(-80, 80) * mm});
            skLineSegment(sketch, "E79.2", {"start": v(-80, -80) * mm, "end": v(-80, 80) * mm});
            skArc(sketch, "E79.3", {"start": v(-80, -80) * mm, "mid": v(-77.07, -87.07) * mm, "end": v(-70, -90) * mm});
            skLineSegment(sketch, "E79.4", {"start": v(-70, -90) * mm, "end": v(70, -90) * mm});
            skArc(sketch, "E79.5", {"start": v(70, -90) * mm, "mid": v(77.07, -87.07) * mm, "end": v(80, -80) * mm});
            skLineSegment(sketch, "E79.6", {"start": v(80, -80) * mm, "end": v(80, 80) * mm});
            skArc(sketch, "E79.7", {"start": v(80, 80) * mm, "mid": v(77.07, 87.07) * mm, "end": v(70, 90) * mm});
            skArc(sketch, "E79.8", {"start": v(56.15, 48.18) * mm, "mid": v(0, 67.5) * mm, "end": v(-56.15, 48.18) * mm});
            skArc(sketch, "E79.9", {"start": v(-56.15, -48.18) * mm, "mid": v(0, -67.5) * mm, "end": v(56.15, -48.18) * mm});
            skLineSegment(sketch, "E79.10", {"start": v(60, 40.3) * mm, "end": v(60, -40.3) * mm});
            skLineSegment(sketch, "E79.11", {"start": v(-60, 40.3) * mm, "end": v(-60, -40.3) * mm});
            skArc(sketch, "E79.12", {"start": v(-56.15, 48.18) * mm, "mid": v(-58.99, 44.68) * mm, "end": v(-60, 40.3) * mm});
            skArc(sketch, "E79.13", {"start": v(-60, -40.3) * mm, "mid": v(-58.99, -44.68) * mm, "end": v(-56.15, -48.18) * mm});
            skArc(sketch, "E79.14", {"start": v(56.15, -48.18) * mm, "mid": v(58.99, -44.68) * mm, "end": v(60, -40.3) * mm});
            skArc(sketch, "E79.15", {"start": v(60, 40.3) * mm, "mid": v(58.99, 44.68) * mm, "end": v(56.15, 48.18) * mm});
            skCircle(sketch, "E79.16", {"center": v(60, 67.5) * mm, "radius": 4 * mm});
            skCircle(sketch, "E79.17", {"center": v(-60, 67.5) * mm, "radius": 4 * mm});
            skCircle(sketch, "E79.18", {"center": v(-60, -67.5) * mm, "radius": 4 * mm});
            skCircle(sketch, "E79.19", {"center": v(60, -67.5) * mm, "radius": 4 * mm});
            skPoint(sketch, "E80.endSnap0", {"position": v(0, 90) * mm});
            skLineSegment(sketch, "E81", {"start": v(0, 90) * mm, "end": v(0, 120) * mm, "construction": true});
            skCircle(sketch, "E82", {"center": v(0, 120) * mm, "radius": 6 * mm});
            skLineSegment(sketch, "E83", {"start": v(-15, 120) * mm, "end": v(-15, 108) * mm});
            skLineSegment(sketch, "E84", {"start": v(15, 120) * mm, "end": v(15, 108) * mm});
            skLineSegment(sketch, "E85", {"start": v(15, 108) * mm, "end": v(33, 90) * mm});
            skLineSegment(sketch, "E86", {"start": v(-15, 108) * mm, "end": v(-33, 90) * mm});
            skArc(sketch, "E87", {"start": v(15, 120) * mm, "mid": v(0, 135) * mm, "end": v(-15, 120) * mm});
            skLineSegment(sketch, "E88", {"start": v(80, 0) * mm, "end": v(-80, 0) * mm, "construction": true});
            skCircle(sketch, "E89.MirrorC", {"center": v(0, -120) * mm, "radius": 6 * mm});
            skLineSegment(sketch, "E90.MirrorCS", {"start": v(0, -90) * mm, "end": v(0, -120) * mm, "construction": true});
            skLineSegment(sketch, "E91.MirrorCS", {"start": v(15, -108) * mm, "end": v(33, -90) * mm});
            skLineSegment(sketch, "E92.MirrorCS", {"start": v(15, -120) * mm, "end": v(15, -108) * mm});
            skArc(sketch, "E93.MirrorCS", {"start": v(15, -120) * mm, "mid": v(0, -135) * mm, "end": v(-15, -120) * mm});
            skLineSegment(sketch, "E94.MirrorCS", {"start": v(-15, -120) * mm, "end": v(-15, -108) * mm});
            skLineSegment(sketch, "E95.MirrorCS", {"start": v(-15, -108) * mm, "end": v(-33, -90) * mm});
            skSolve(sketch);
        }
        {
            var Q0;
            Q0 = qSketchRegion(id + "F16", true);
            var Q1;
            Q1=makeQuery(id+"F2.opExtrude","CAP_FACE",FACE,{"disambiguationData":[OSD([sQuery(id+"F0.wireOp",EDGE,"E12"),sQuery(id+"F0.wireOp",EDGE,"E13"),sQuery(id+"F0.wireOp",EDGE,"E14"),sQuery(id+"F0.wireOp",EDGE,"E15"),sQuery(id+"F0.wireOp",EDGE,"E17.filletArc"),sQuery(id+"F0.wireOp",EDGE,"E18.filletArc"),sQuery(id+"F0.wireOp",EDGE,"E19.filletArc"),sQuery(id+"F0.wireOp",EDGE,"E20.filletArc"),sQuery(id+"F0.wireOp",EDGE,"E25.0"),sQuery(id+"F0.wireOp",EDGE,"E25.1"),sQuery(id+"F0.wireOp",EDGE,"E25.2"),sQuery(id+"F0.wireOp",EDGE,"E25.3"),sQuery(id+"F0.wireOp",EDGE,"E25.4"),sQuery(id+"F0.wireOp",EDGE,"E25.5"),sQuery(id+"F0.wireOp",EDGE,"E25.6"),sQuery(id+"F0.wireOp",EDGE,"E25.7")])],"isStart":false});
            extrude(context, id + "F17", {"entities" : qUnion([Q0]), "endBound" : BoundingType.UP_TO_SURFACE, "endBoundEntityFace" : qUnion([Q1]), "depth" : 25 * mm});
        }
    });
